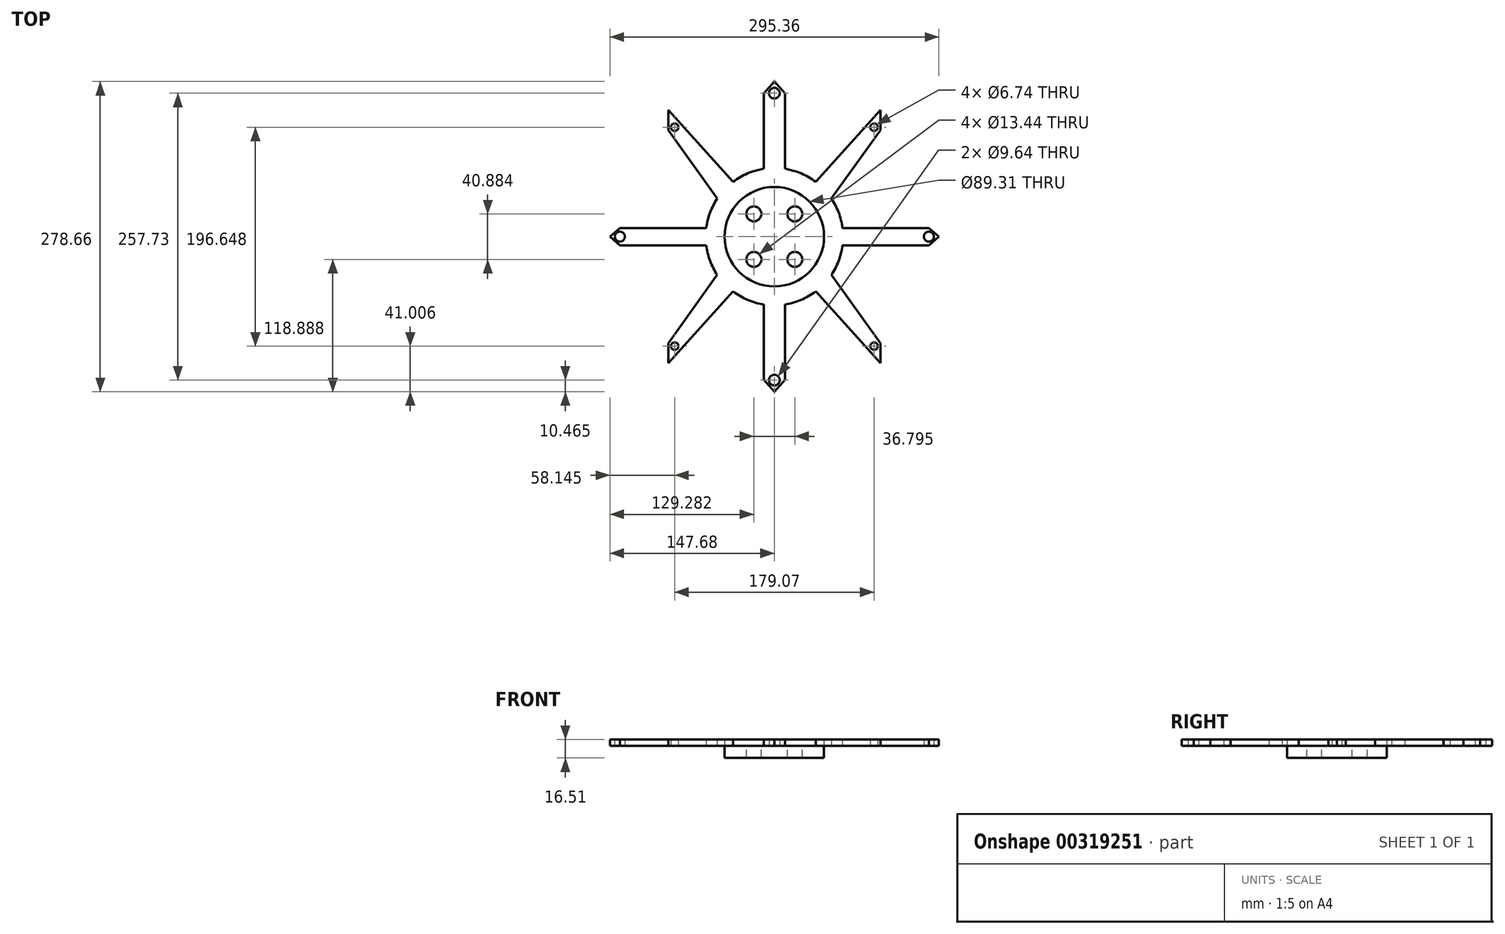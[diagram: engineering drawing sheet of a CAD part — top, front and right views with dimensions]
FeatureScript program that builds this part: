
annotation { "Feature Type Name" : "Feature", "Feature Type Description" : "" }
export const myFeature = defineFeature(function(context is Context, id is Id, definition is map)
    precondition{}
    {
        {
            var Q0;
            Q0=qCreatedBy(makeId("Top.planeOp"),FACE);
            var sketch = newSketch(context, id + "F0", { "sketchPlane" : qUnion([Q0])});
            skCircle(sketch, "E0", {"center": v(0, 0) * mm, "radius": 61.66 * mm});
            skLineSegment(sketch, "E1", {"start": v(-51.22, 34.32) * mm, "end": v(-95.28, 95.74) * mm});
            skLineSegment(sketch, "E2", {"start": v(-95.28, 95.74) * mm, "end": v(-95.28, 113.64) * mm});
            skLineSegment(sketch, "E3", {"start": v(-95.28, 113.64) * mm, "end": v(-37.13, 49.22) * mm});
            skLineSegment(sketch, "E4.MirrorCS", {"start": v(95.28, 113.64) * mm, "end": v(37.13, 49.22) * mm});
            skLineSegment(sketch, "E5.MirrorCS", {"start": v(51.22, 34.32) * mm, "end": v(95.28, 95.74) * mm});
            skLineSegment(sketch, "E6.MirrorCS", {"start": v(95.28, 95.74) * mm, "end": v(95.28, 113.64) * mm});
            skLineSegment(sketch, "E7.MirrorCS", {"start": v(-51.22, -34.32) * mm, "end": v(-95.28, -95.74) * mm});
            skLineSegment(sketch, "E8.MirrorCS", {"start": v(-95.28, -113.64) * mm, "end": v(-37.13, -49.22) * mm});
            skLineSegment(sketch, "E9.MirrorCS", {"start": v(-95.28, -95.74) * mm, "end": v(-95.28, -113.64) * mm});
            skLineSegment(sketch, "E10.MirrorCS", {"start": v(51.22, -34.32) * mm, "end": v(95.28, -95.74) * mm});
            skLineSegment(sketch, "E11.MirrorCS", {"start": v(95.28, -113.64) * mm, "end": v(37.13, -49.22) * mm});
            skLineSegment(sketch, "E12.MirrorCS", {"start": v(95.28, -95.74) * mm, "end": v(95.28, -113.64) * mm});
            skLineSegment(sketch, "E13", {"start": v(-9.58, 60.9) * mm, "end": v(-9.58, 128.57) * mm});
            skLineSegment(sketch, "E14", {"start": v(-9.58, 128.57) * mm, "end": v(0, 139.33) * mm});
            skLineSegment(sketch, "E15.MirrorCS", {"start": v(9.58, 60.9) * mm, "end": v(9.58, 128.57) * mm});
            skLineSegment(sketch, "E16.MirrorCS", {"start": v(9.58, 128.57) * mm, "end": v(0, 139.33) * mm});
            skLineSegment(sketch, "E17.MirrorCS", {"start": v(9.58, -60.9) * mm, "end": v(9.58, -128.57) * mm});
            skLineSegment(sketch, "E18.MirrorCS", {"start": v(-9.58, -60.9) * mm, "end": v(-9.58, -128.57) * mm});
            skLineSegment(sketch, "E19.MirrorCS", {"start": v(-9.58, -128.57) * mm, "end": v(0, -139.33) * mm});
            skLineSegment(sketch, "E20.MirrorCS", {"start": v(9.58, -128.57) * mm, "end": v(0, -139.33) * mm});
            skLineSegment(sketch, "E21", {"start": v(61.16, 7.77) * mm, "end": v(138.79, 7.77) * mm});
            skLineSegment(sketch, "E22", {"start": v(138.79, 7.77) * mm, "end": v(147.68, 0) * mm});
            skLineSegment(sketch, "E23.MirrorCS", {"start": v(138.79, -7.77) * mm, "end": v(147.68, 0) * mm});
            skLineSegment(sketch, "E24.MirrorCS", {"start": v(61.16, -7.77) * mm, "end": v(138.79, -7.77) * mm});
            skLineSegment(sketch, "E25.MirrorCS", {"start": v(-61.16, 7.77) * mm, "end": v(-138.79, 7.77) * mm});
            skLineSegment(sketch, "E26.MirrorCS", {"start": v(-61.16, -7.77) * mm, "end": v(-138.79, -7.77) * mm});
            skLineSegment(sketch, "E27.MirrorCS", {"start": v(-138.79, -7.77) * mm, "end": v(-147.68, 0) * mm});
            skLineSegment(sketch, "E28.MirrorCS", {"start": v(-138.79, 7.77) * mm, "end": v(-147.68, 0) * mm});
            skCircle(sketch, "E29", {"center": v(0, 0) * mm, "radius": 44.65 * mm});
            skCircle(sketch, "E30", {"center": v(0, 128.86) * mm, "radius": 4.82 * mm});
            skCircle(sketch, "E31.MirrorC", {"center": v(0, -128.86) * mm, "radius": 4.82 * mm});
            skCircle(sketch, "E32", {"center": v(-138.79, 0) * mm, "radius": 4.5 * mm});
            skCircle(sketch, "E33", {"center": v(-89.54, 98.32) * mm, "radius": 3.37 * mm});
            skCircle(sketch, "E34.MirrorC", {"center": v(138.79, 0) * mm, "radius": 4.5 * mm});
            skCircle(sketch, "E35.MirrorC", {"center": v(89.54, 98.32) * mm, "radius": 3.37 * mm});
            skCircle(sketch, "E36.MirrorC", {"center": v(89.54, -98.32) * mm, "radius": 3.37 * mm});
            skCircle(sketch, "E37.MirrorC", {"center": v(-89.54, -98.32) * mm, "radius": 3.37 * mm});
            skCircle(sketch, "E38", {"center": v(-18.4, 20.44) * mm, "radius": 6.72 * mm});
            skCircle(sketch, "E39.MirrorC", {"center": v(18.4, 20.44) * mm, "radius": 6.72 * mm});
            skCircle(sketch, "E40.MirrorC", {"center": v(18.4, -20.44) * mm, "radius": 6.72 * mm});
            skCircle(sketch, "E41.MirrorC", {"center": v(-18.4, -20.44) * mm, "radius": 6.72 * mm});
            skSolve(sketch);
        }
        {
            var Q0;
            Q0=makeQuery(id+"F0.imprint","IMPRINT",FACE,{"disambiguationData":[TD([[makeQuery(id+"F0.imprint","IMPRINT",EDGE,{"derivedFrom":sQuery(id+"F0.wireOp",EDGE,"E29")}),1.0]])]});
            extrude(context, id + "F1", {"entities" : qUnion([Q0]), "oppositeDirection" : true, "depth" : 10.92 * mm});
        }
        {
            var Q0;
            {var subQ0=sQuery(id+"F0.wireOp",EDGE,"E0");var subQ8=makeQuery(id+"F0.imprint","INTERSECT",VERTEX,{"derivedFrom":[subQ0,sQuery(id+"F0.wireOp",EDGE,"E5.MirrorCS")]});Q0=makeQuery(id+"F0.imprint","IMPRINT",FACE,{"disambiguationData":[TD([[makeQuery(id+"F0.imprint","IMPRINT",EDGE,{"disambiguationData":[TD([[subQ8,1.0]])],"derivedFrom":subQ0}),1.0]])]});}
            var Q1;
            {var subQ1=sQuery(id+"F0.wireOp",EDGE,"E13");Q1=makeQuery(id+"F0.imprint","IMPRINT",FACE,{"disambiguationData":[TD([[makeQuery(id+"F0.imprint","IMPRINT",EDGE,{"derivedFrom":subQ1}),-1.0]])]});}
            var Q2;
            {var subQ0=sQuery(id+"F0.wireOp",EDGE,"E4.MirrorCS");Q2=makeQuery(id+"F0.imprint","IMPRINT",FACE,{"disambiguationData":[TD([[makeQuery(id+"F0.imprint","IMPRINT",EDGE,{"derivedFrom":subQ0}),1.0]])]});}
            var Q3;
            {var subQ0=sQuery(id+"F0.wireOp",EDGE,"E21");Q3=makeQuery(id+"F0.imprint","IMPRINT",FACE,{"disambiguationData":[TD([[makeQuery(id+"F0.imprint","IMPRINT",EDGE,{"derivedFrom":subQ0}),-1.0]])]});}
            var Q4;
            {var subQ0=sQuery(id+"F0.wireOp",EDGE,"E10.MirrorCS");Q4=makeQuery(id+"F0.imprint","IMPRINT",FACE,{"disambiguationData":[TD([[makeQuery(id+"F0.imprint","IMPRINT",EDGE,{"derivedFrom":subQ0}),-1.0]])]});}
            var Q5;
            {var subQ1=sQuery(id+"F0.wireOp",EDGE,"E17.MirrorCS");Q5=makeQuery(id+"F0.imprint","IMPRINT",FACE,{"disambiguationData":[TD([[makeQuery(id+"F0.imprint","IMPRINT",EDGE,{"derivedFrom":subQ1}),-1.0]])]});}
            var Q6;
            {var subQ0=sQuery(id+"F0.wireOp",EDGE,"E7.MirrorCS");Q6=makeQuery(id+"F0.imprint","IMPRINT",FACE,{"disambiguationData":[TD([[makeQuery(id+"F0.imprint","IMPRINT",EDGE,{"derivedFrom":subQ0}),1.0]])]});}
            var Q7;
            {var subQ1=sQuery(id+"F0.wireOp",EDGE,"E25.MirrorCS");Q7=makeQuery(id+"F0.imprint","IMPRINT",FACE,{"disambiguationData":[TD([[makeQuery(id+"F0.imprint","IMPRINT",EDGE,{"derivedFrom":subQ1}),1.0]])]});}
            var Q8;
            {var subQ0=sQuery(id+"F0.wireOp",EDGE,"E1");Q8=makeQuery(id+"F0.imprint","IMPRINT",FACE,{"disambiguationData":[TD([[makeQuery(id+"F0.imprint","IMPRINT",EDGE,{"derivedFrom":subQ0}),-1.0]])]});}
            extrude(context, id + "F2", {"entities" : qUnion([Q0, Q1, Q2, Q3, Q4, Q5, Q6, Q7, Q8]), "depth" : 5.6 * mm});
        }
    });
